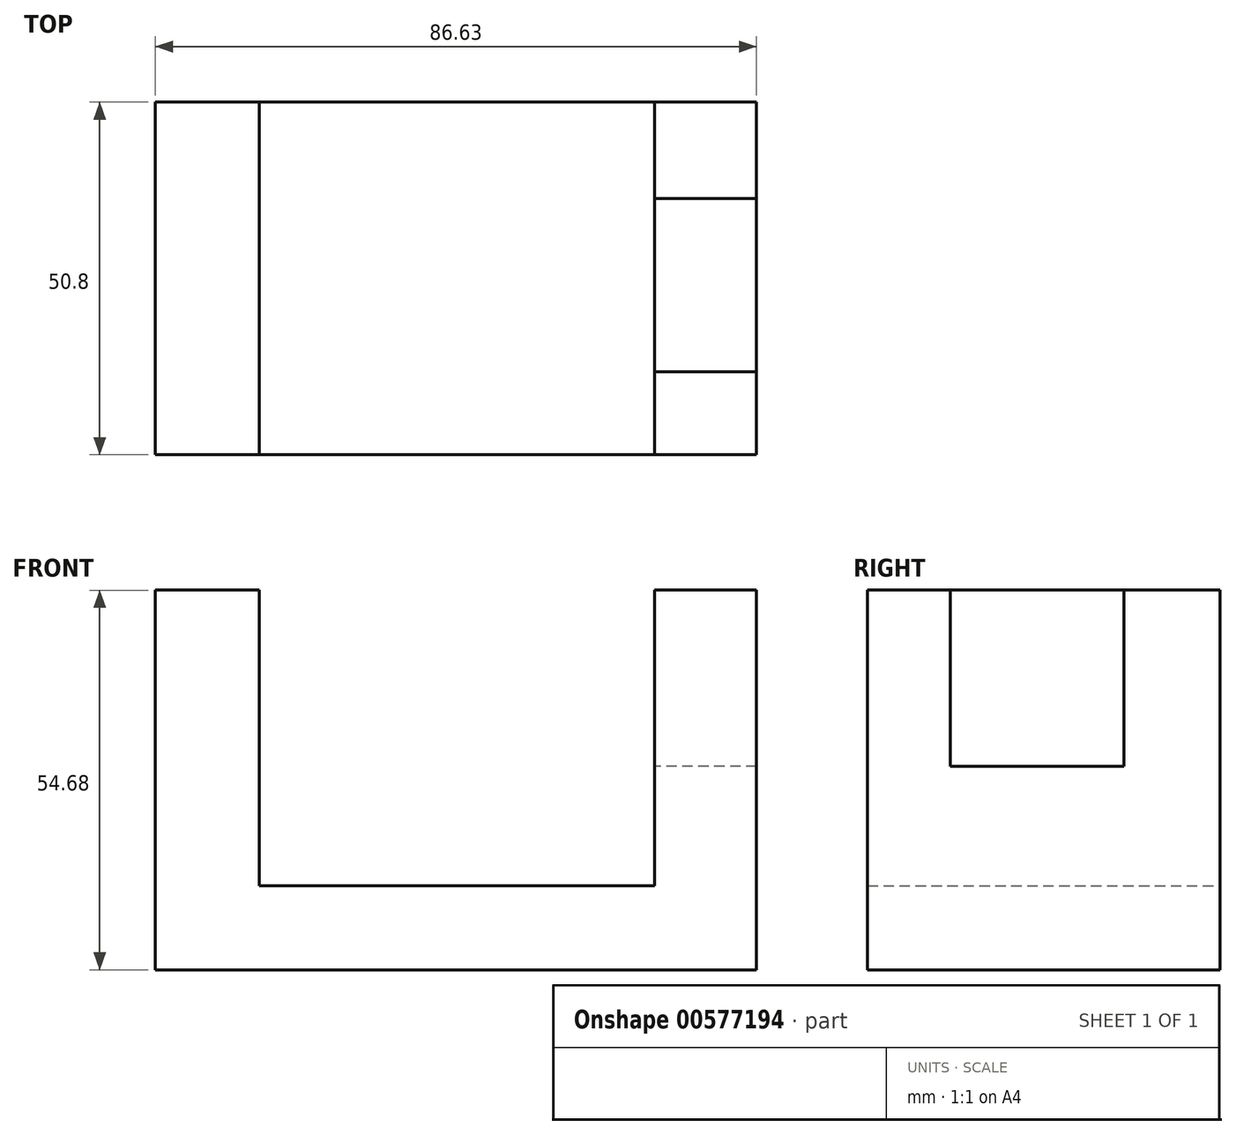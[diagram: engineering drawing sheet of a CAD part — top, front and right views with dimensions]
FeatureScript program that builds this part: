
annotation { "Feature Type Name" : "Feature", "Feature Type Description" : "" }
export const myFeature = defineFeature(function(context is Context, id is Id, definition is map)
    precondition{}
    {
        {
            var Q0;
            Q0=qCreatedBy(makeId("Front.planeOp"),FACE);
            var sketch = newSketch(context, id + "F0", { "sketchPlane" : qUnion([Q0])});
            skLineSegment(sketch, "E0.bottom", {"start": v(0, 0) * mm, "end": v(86.63, 0) * mm});
            skLineSegment(sketch, "E0.top", {"start": v(0, 54.68) * mm, "end": v(14.97, 54.68) * mm});
            skLineSegment(sketch, "E0.left", {"start": v(0, 0) * mm, "end": v(0, 54.68) * mm});
            skLineSegment(sketch, "E0.right", {"start": v(86.63, 0) * mm, "end": v(86.63, 54.68) * mm});
            skLineSegment(sketch, "E1.top", {"start": v(14.97, 12.09) * mm, "end": v(71.95, 12.09) * mm});
            skLineSegment(sketch, "E1.left", {"start": v(14.97, 54.68) * mm, "end": v(14.97, 12.09) * mm});
            skLineSegment(sketch, "E1.right", {"start": v(71.95, 54.68) * mm, "end": v(71.95, 12.09) * mm});
            skLineSegment(sketch, "E2.trimOffspring", {"start": v(71.95, 54.68) * mm, "end": v(86.63, 54.68) * mm});
            skSolve(sketch);
        }
        {
            var Q0;
            Q0 = qSketchRegion(id + "F0", true);
            extrude(context, id + "F1", {"entities" : qUnion([Q0]), "depth" : 50.8 * mm, "offsetDistance" : 25.4 * mm});
        }
        {
            var Q0;
            Q0=makeQuery(id+"F1.opExtrude","SWEPT_FACE",FACE,{"disambiguationData":[OSD([sQuery(id+"F0.wireOp",EDGE,"E2.trimOffspring")])]});
            var sketch = newSketch(context, id + "F2", { "sketchPlane" : qUnion([Q0])});
            skLineSegment(sketch, "E3.bottom", {"start": v(71.95, -33.92) * mm, "end": v(86.63, -33.92) * mm});
            skLineSegment(sketch, "E3.top", {"start": v(71.95, -13.88) * mm, "end": v(86.63, -13.88) * mm});
            skLineSegment(sketch, "E3.left", {"start": v(71.95, -33.92) * mm, "end": v(71.95, -13.88) * mm});
            skLineSegment(sketch, "E3.right", {"start": v(86.63, -33.92) * mm, "end": v(86.63, -13.88) * mm});
            skLineSegment(sketch, "E4.bottom", {"start": v(86.63, -13.88) * mm, "end": v(71.95, -13.88) * mm});
            skLineSegment(sketch, "E4.top", {"start": v(86.63, -38.85) * mm, "end": v(71.95, -38.85) * mm});
            skLineSegment(sketch, "E4.left", {"start": v(86.63, -13.88) * mm, "end": v(86.63, -38.85) * mm});
            skLineSegment(sketch, "E4.right", {"start": v(71.95, -13.88) * mm, "end": v(71.95, -38.85) * mm});
            skSolve(sketch);
        }
        {
            var Q0;
            Q0 = qSketchRegion(id + "F2", true);
            extrude(context, id + "F3", {"entities" : qUnion([Q0]), "operationType" : NewBodyOperationType.REMOVE, "oppositeDirection" : true, "depth" : 25.4 * mm, "offsetDistance" : 25.4 * mm});
        }
    });
